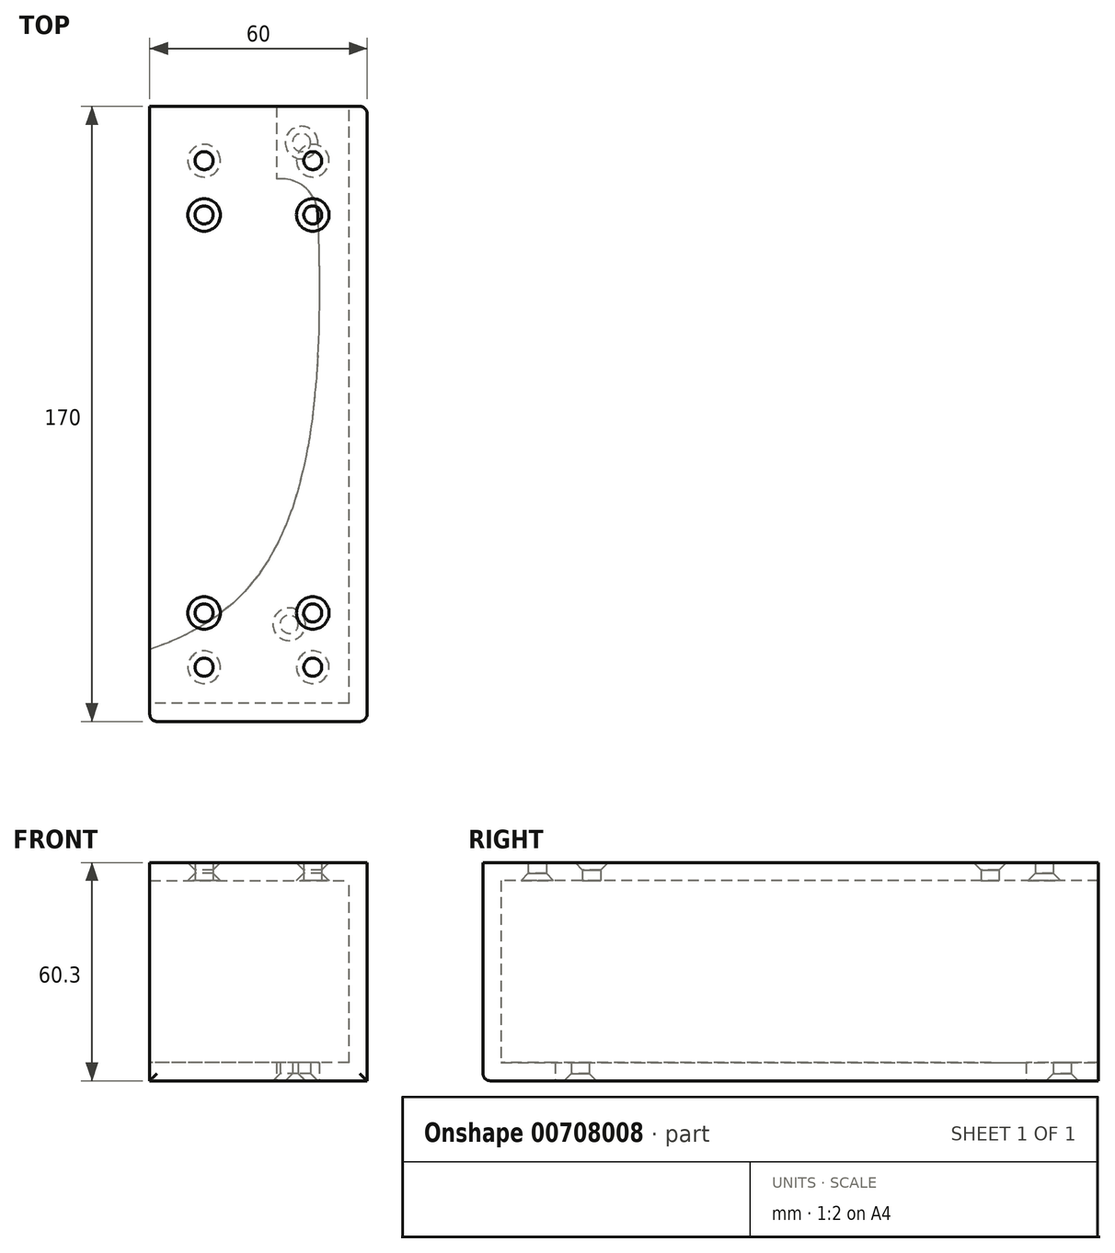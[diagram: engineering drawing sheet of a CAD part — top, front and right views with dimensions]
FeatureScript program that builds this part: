
annotation { "Feature Type Name" : "Feature", "Feature Type Description" : "" }
export const myFeature = defineFeature(function(context is Context, id is Id, definition is map)
    precondition{}
    {
        {
            var Q0;
            Q0=qCreatedBy(makeId("Top.planeOp"),FACE);
            var sketch = newSketch(context, id + "F0", { "sketchPlane" : qUnion([Q0])});
            skLineSegment(sketch, "E0.bottom", {"start": v(0, 0) * mm, "end": v(-60, 0) * mm});
            skLineSegment(sketch, "E0.top", {"start": v(0, 170) * mm, "end": v(-15, 170) * mm});
            skLineSegment(sketch, "E0.left", {"start": v(0, 0) * mm, "end": v(0, 170) * mm});
            skFitSpline(sketch, "E1", {"points": [v(-15, 170) * mm, v(-35.25, 34.39) * mm, v(-170, 15) * mm], "startDerivative": vector(17.06, -328.82) * mm, "endDerivative": vector(-327.27, 19.02) * mm});
            skCircle(sketch, "E2", {"center": v(-21.5, 26.87) * mm, "radius": 2.5 * mm});
            skCircle(sketch, "E3", {"center": v(-18.1, 160) * mm, "radius": 2.5 * mm});
            skLineSegment(sketch, "E4.bottom", {"start": v(0, 170) * mm, "end": v(-25, 170) * mm});
            skLineSegment(sketch, "E4.top", {"start": v(-23.62, 150) * mm, "end": v(-25, 150) * mm});
            skLineSegment(sketch, "E4.left", {"start": v(0, 170) * mm, "end": v(0, 150) * mm});
            skLineSegment(sketch, "E4.right", {"start": v(-25, 170) * mm, "end": v(-25, 150) * mm});
            skPoint(sketch, "E5.visualSharp", {"position": v(-150, 13.89) * mm});
            skPoint(sketch, "E6.visualSharp", {"position": v(-14.01, 150) * mm});
            skArc(sketch, "E6.filletArc", {"start": v(-13.62, 140.35) * mm, "mid": v(-16.67, 147.2) * mm, "end": v(-23.62, 150) * mm});
            skLineSegment(sketch, "E7", {"start": v(-60, 19.91) * mm, "end": v(-60, 0) * mm});
            skSolve(sketch);
        }
        {
            var Q0;
            Q0 = qSketchRegion(id + "F0", true);
            extrude(context, id + "F1", {"entities" : qUnion([Q0]), "depth" : 5 * mm, "offsetDistance" : 25 * mm});
        }
        {
            var Q0;
            Q0=makeQuery(id+"F1.opExtrude","SWEPT_FACE",FACE,{"disambiguationData":[OSD([sQuery(id+"F0.wireOp",EDGE,"E0.left")])]});
            var sketch = newSketch(context, id + "F2", { "sketchPlane" : qUnion([Q0])});
            skLineSegment(sketch, "E8.bottom", {"start": v(0, 5) * mm, "end": v(170, 5) * mm});
            skLineSegment(sketch, "E8.top", {"start": v(0, 55.3) * mm, "end": v(170, 55.3) * mm});
            skLineSegment(sketch, "E8.left", {"start": v(0, 5) * mm, "end": v(0, 55.3) * mm});
            skLineSegment(sketch, "E8.right", {"start": v(170, 5) * mm, "end": v(170, 55.3) * mm});
            skSolve(sketch);
        }
        {
            var Q0;
            Q0=makeQuery(id+"F2.imprint","IMPRINT",FACE,{"disambiguationData":[TD([[makeQuery(id+"F2.imprint","IMPRINT",EDGE,{"derivedFrom":sQuery(id+"F2.wireOp",EDGE,"E8.bottom")}),1.0]])]});
            extrude(context, id + "F3", {"entities" : qUnion([Q0]), "operationType" : NewBodyOperationType.ADD, "depth" : -5 * mm, "offsetDistance" : 25 * mm});
        }
        {
            var Q0;
            Q0=makeQuery(id+"F3.boolean.opBoolean","MERGE",FACE,{"derivedFrom":[makeQuery(id+"F1.opExtrude","SWEPT_FACE",FACE,{"disambiguationData":[OSD([sQuery(id+"F0.wireOp",EDGE,"E0.bottom")])]}),makeQuery(id+"F3.opExtrude","SWEPT_FACE",FACE,{"disambiguationData":[OSD([sQuery(id+"F2.wireOp",EDGE,"E8.left")])]})]});
            var sketch = newSketch(context, id + "F4", { "sketchPlane" : qUnion([Q0])});
            skLineSegment(sketch, "E9.bottom", {"start": v(-5, 5) * mm, "end": v(-60, 5) * mm});
            skLineSegment(sketch, "E9.top", {"start": v(-5, 55.3) * mm, "end": v(-60, 55.3) * mm});
            skLineSegment(sketch, "E9.left", {"start": v(-5, 5) * mm, "end": v(-5, 55.3) * mm});
            skLineSegment(sketch, "E10", {"start": v(-60, 55.3) * mm, "end": v(-60, 5) * mm});
            skSolve(sketch);
        }
        {
            var Q0;
            Q0 = qSketchRegion(id + "F4", true);
            extrude(context, id + "F5", {"entities" : qUnion([Q0]), "operationType" : NewBodyOperationType.ADD, "depth" : -5 * mm, "offsetDistance" : 25 * mm});
        }
        {
            var Q0;
            Q0=makeQuery(id+"F5.boolean.opBoolean","MERGE",FACE,{"derivedFrom":[makeQuery(id+"F3.opExtrude","SWEPT_FACE",FACE,{"disambiguationData":[OSD([sQuery(id+"F2.wireOp",EDGE,"E8.top")])]}),makeQuery(id+"F5.opExtrude","SWEPT_FACE",FACE,{"disambiguationData":[OSD([sQuery(id+"F4.wireOp",EDGE,"E9.top")])]})]});
            var sketch = newSketch(context, id + "F6", { "sketchPlane" : qUnion([Q0])});
            skLineSegment(sketch, "E11.bottom", {"start": v(0, 0) * mm, "end": v(-60, 0) * mm});
            skLineSegment(sketch, "E11.top", {"start": v(0, 170) * mm, "end": v(-60, 170) * mm});
            skLineSegment(sketch, "E11.left", {"start": v(0, 0) * mm, "end": v(0, 170) * mm});
            skLineSegment(sketch, "E11.right", {"start": v(-60, 0) * mm, "end": v(-60, 170) * mm});
            skSolve(sketch);
        }
        {
            var Q0;
            {var subQ4=sQuery(id+"F6.wireOp",EDGE,"E11.bottom");Q0=makeQuery(id+"F6.imprint","IMPRINT",FACE,{"disambiguationData":[TD([[makeQuery(id+"F6.imprint","IMPRINT",EDGE,{"derivedFrom":subQ4}),1.0]])]});}
            var sketch = newSketch(context, id + "F7", { "sketchPlane" : qUnion([Q0])});
            skLineSegment(sketch, "E12.bottom", {"start": v(0, 0) * mm, "end": v(-60, 0) * mm});
            skLineSegment(sketch, "E12.top", {"start": v(0, 170) * mm, "end": v(-60, 170) * mm});
            skLineSegment(sketch, "E12.left", {"start": v(0, 0) * mm, "end": v(0, 170) * mm});
            skLineSegment(sketch, "E12.right", {"start": v(-60, 0) * mm, "end": v(-60, 170) * mm});
            skLineSegment(sketch, "E13.bottom", {"start": v(0, 170) * mm, "end": v(-15, 170) * mm});
            skLineSegment(sketch, "E13.top", {"start": v(0, 155) * mm, "end": v(-15, 155) * mm, "construction": true});
            skLineSegment(sketch, "E13.left", {"start": v(0, 170) * mm, "end": v(0, 155) * mm});
            skLineSegment(sketch, "E13.right", {"start": v(-15, 170) * mm, "end": v(-15, 155) * mm, "construction": true});
            skLineSegment(sketch, "E14.bottom", {"start": v(0, 0) * mm, "end": v(-15, 0) * mm});
            skLineSegment(sketch, "E14.top", {"start": v(0, 15) * mm, "end": v(-15, 15) * mm, "construction": true});
            skLineSegment(sketch, "E14.left", {"start": v(0, 0) * mm, "end": v(0, 15) * mm});
            skLineSegment(sketch, "E14.right", {"start": v(-15, 0) * mm, "end": v(-15, 15) * mm, "construction": true});
            skLineSegment(sketch, "E15.bottom", {"start": v(-60, 0) * mm, "end": v(-45, 0) * mm});
            skLineSegment(sketch, "E15.top", {"start": v(-60, 15) * mm, "end": v(-45, 15) * mm, "construction": true});
            skLineSegment(sketch, "E15.left", {"start": v(-60, 0) * mm, "end": v(-60, 15) * mm});
            skLineSegment(sketch, "E15.right", {"start": v(-45, 0) * mm, "end": v(-45, 15) * mm, "construction": true});
            skLineSegment(sketch, "E16.bottom", {"start": v(-60, 170) * mm, "end": v(-45, 170) * mm});
            skLineSegment(sketch, "E16.top", {"start": v(-60, 155) * mm, "end": v(-45, 155) * mm, "construction": true});
            skLineSegment(sketch, "E16.left", {"start": v(-60, 170) * mm, "end": v(-60, 155) * mm});
            skLineSegment(sketch, "E16.right", {"start": v(-45, 170) * mm, "end": v(-45, 155) * mm, "construction": true});
            skCircle(sketch, "E17", {"center": v(-15, 155) * mm, "radius": 2.5 * mm});
            skCircle(sketch, "E18", {"center": v(-45, 155) * mm, "radius": 2.5 * mm});
            skCircle(sketch, "E19", {"center": v(-15, 15) * mm, "radius": 2.5 * mm});
            skCircle(sketch, "E20", {"center": v(-45, 15) * mm, "radius": 2.5 * mm});
            skLineSegment(sketch, "E21", {"start": v(-15, 15) * mm, "end": v(-15, 30) * mm, "construction": true});
            skLineSegment(sketch, "E22", {"start": v(-45, 15) * mm, "end": v(-45, 30) * mm, "construction": true});
            skLineSegment(sketch, "E23", {"start": v(-15, 155) * mm, "end": v(-15, 140) * mm, "construction": true});
            skLineSegment(sketch, "E24", {"start": v(-45, 155) * mm, "end": v(-45, 140) * mm, "construction": true});
            skCircle(sketch, "E25", {"center": v(-15, 140) * mm, "radius": 2.5 * mm});
            skCircle(sketch, "E26", {"center": v(-45, 140) * mm, "radius": 2.5 * mm});
            skCircle(sketch, "E27", {"center": v(-45, 30) * mm, "radius": 2.5 * mm});
            skCircle(sketch, "E28", {"center": v(-15, 30) * mm, "radius": 2.5 * mm});
            skSolve(sketch);
        }
        {
            var Q0;
            Q0 = qSketchRegion(id + "F7", true);
            extrude(context, id + "F8", {"entities" : qUnion([Q0]), "operationType" : NewBodyOperationType.ADD, "depth" : 5 * mm, "offsetDistance" : 25 * mm});
        }
        {
            var Q0;
            Q0=makeQuery(id+"F8.opExtrude","CAP_EDGE",EDGE,{"disambiguationData":[OSD([sQuery(id+"F7.wireOp",EDGE,"E25")])],"isStart":false});
            var Q1;
            Q1=makeQuery(id+"F8.opExtrude","CAP_EDGE",EDGE,{"disambiguationData":[OSD([sQuery(id+"F7.wireOp",EDGE,"E26")])],"isStart":false});
            var Q2;
            Q2=makeQuery(id+"F8.opExtrude","CAP_EDGE",EDGE,{"disambiguationData":[OSD([sQuery(id+"F7.wireOp",EDGE,"E28")])],"isStart":false});
            var Q3;
            Q3=makeQuery(id+"F8.opExtrude","CAP_EDGE",EDGE,{"disambiguationData":[OSD([sQuery(id+"F7.wireOp",EDGE,"E27")])],"isStart":false});
            chamfer(context, id + "F9", {"entities" : qUnion([Q0, Q1, Q2, Q3]), "width" : 2 * mm, "tangentPropagation" : true});
        }
        {
            var Q0;
            Q0=makeQuery(id+"F8.opExtrude","CAP_EDGE",EDGE,{"disambiguationData":[OSD([sQuery(id+"F7.wireOp",EDGE,"E18")])],"isStart":true});
            var Q1;
            Q1=makeQuery(id+"F8.opExtrude","CAP_EDGE",EDGE,{"disambiguationData":[OSD([sQuery(id+"F7.wireOp",EDGE,"E17")])],"isStart":true});
            var Q2;
            Q2=makeQuery(id+"F8.opExtrude","CAP_EDGE",EDGE,{"disambiguationData":[OSD([sQuery(id+"F7.wireOp",EDGE,"E20")])],"isStart":true});
            var Q3;
            Q3=makeQuery(id+"F8.opExtrude","CAP_EDGE",EDGE,{"disambiguationData":[OSD([sQuery(id+"F7.wireOp",EDGE,"E19")])],"isStart":true});
            chamfer(context, id + "F10", {"entities" : qUnion([Q0, Q1, Q2, Q3]), "width" : 2 * mm, "tangentPropagation" : true});
        }
        {
            var Q0;
            Q0=makeQuery(id+"F1.opExtrude","CAP_EDGE",EDGE,{"disambiguationData":[OSD([sQuery(id+"F0.wireOp",EDGE,"E2")])],"isStart":true});
            var Q1;
            Q1=makeQuery(id+"F1.opExtrude","CAP_EDGE",EDGE,{"disambiguationData":[OSD([sQuery(id+"F0.wireOp",EDGE,"E3")])],"isStart":true});
            var Q2;
            Q2=makeQuery(id+"F1.opExtrude","CAP_EDGE",EDGE,{"disambiguationData":[OSD([sQuery(id+"F0.wireOp",EDGE,"602ekmY3-djV7-0EYo-3G5f-2V9RUtqw9AcJ")])],"isStart":true});
            chamfer(context, id + "F11", {"entities" : qUnion([Q0, Q1, Q2]), "width" : 2 * mm, "tangentPropagation" : true});
        }
        {
            var Q0;
            Q0=makeQuery(id+"F8.boolean.opBoolean","MERGE",EDGE,{"derivedFrom":[makeQuery(id+"F3.boolean.opBoolean","MERGE",EDGE,{"derivedFrom":[makeQuery(id+"F1.opExtrude","SWEPT_EDGE",EDGE,{"disambiguationData":[OSD([sQuery(id+"F0.wireOp",EDGE,"E0.bottom"),sQuery(id+"F0.wireOp",EDGE,"E0.left")])]}),makeQuery(id+"F3.opExtrude","CAP_EDGE",EDGE,{"disambiguationData":[OSD([sQuery(id+"F2.wireOp",EDGE,"E8.left")])],"isStart":true})]}),makeQuery(id+"F8.opExtrude","SWEPT_EDGE",EDGE,{"disambiguationData":[OSD([sQuery(id+"F7.wireOp",EDGE,"E14.bottom"),sQuery(id+"F7.wireOp",EDGE,"E14.left")])]})]});
            var Q1;
            Q1=makeQuery(id+"F8.opExtrude","SWEPT_EDGE",EDGE,{"disambiguationData":[OSD([sQuery(id+"F7.wireOp",EDGE,"E15.bottom"),sQuery(id+"F7.wireOp",EDGE,"E15.left")])]});
            var Q2;
            Q2=makeQuery(id+"F5.opExtrude","CAP_EDGE",EDGE,{"disambiguationData":[OSD([sQuery(id+"F4.wireOp",EDGE,"uduKuWtT-cO4U-pCKe-B4Cu-s4ce6nYD45D1")])],"isStart":true});
            var Q3;
            Q3=makeQuery(id+"F5.boolean.opBoolean","MERGE",EDGE,{"derivedFrom":[makeQuery(id+"F1.opExtrude","SWEPT_EDGE",EDGE,{"disambiguationData":[OSD([sQuery(id+"F0.wireOp",EDGE,"E0.bottom"),sQuery(id+"F0.wireOp",EDGE,"OZDD4q5u-z9Ca-XiRg-jXSI-U4c8fKiU3yoC")])]}),makeQuery(id+"F5.opExtrude","CAP_EDGE",EDGE,{"disambiguationData":[OSD([sQuery(id+"F4.wireOp",EDGE,"E9.right")])],"isStart":true})]});
            var Q4;
            Q4=makeQuery(id+"F1.opExtrude","CAP_EDGE",EDGE,{"disambiguationData":[OSD([sQuery(id+"F0.wireOp",EDGE,"E0.bottom")])],"isStart":true});
            var Q5;
            Q5=makeQuery(id+"F8.boolean.opBoolean","MERGE",EDGE,{"derivedFrom":[makeQuery(id+"F3.boolean.opBoolean","MERGE",EDGE,{"derivedFrom":[makeQuery(id+"F1.opExtrude","SWEPT_EDGE",EDGE,{"disambiguationData":[OSD([sQuery(id+"F0.wireOp",EDGE,"E0.left"),sQuery(id+"F0.wireOp",EDGE,"E0.top")])]}),makeQuery(id+"F3.opExtrude","CAP_EDGE",EDGE,{"disambiguationData":[OSD([sQuery(id+"F2.wireOp",EDGE,"E8.right")])],"isStart":true})]}),makeQuery(id+"F8.opExtrude","SWEPT_EDGE",EDGE,{"disambiguationData":[OSD([sQuery(id+"F7.wireOp",EDGE,"E13.bottom"),sQuery(id+"F7.wireOp",EDGE,"E13.left")])]})]});
            var Q6;
            Q6=makeQuery(id+"F8.opExtrude","SWEPT_EDGE",EDGE,{"disambiguationData":[OSD([sQuery(id+"F7.wireOp",EDGE,"E16.bottom"),sQuery(id+"F7.wireOp",EDGE,"E16.left")])]});
            fillet(context, id + "F12", {"entities" : qUnion([Q0, Q1, Q2, Q3, Q4, Q5, Q6]), "radius" : 2 * mm, "tangentPropagation" : true, "allowEdgeOverflow" : false});
        }
    });
